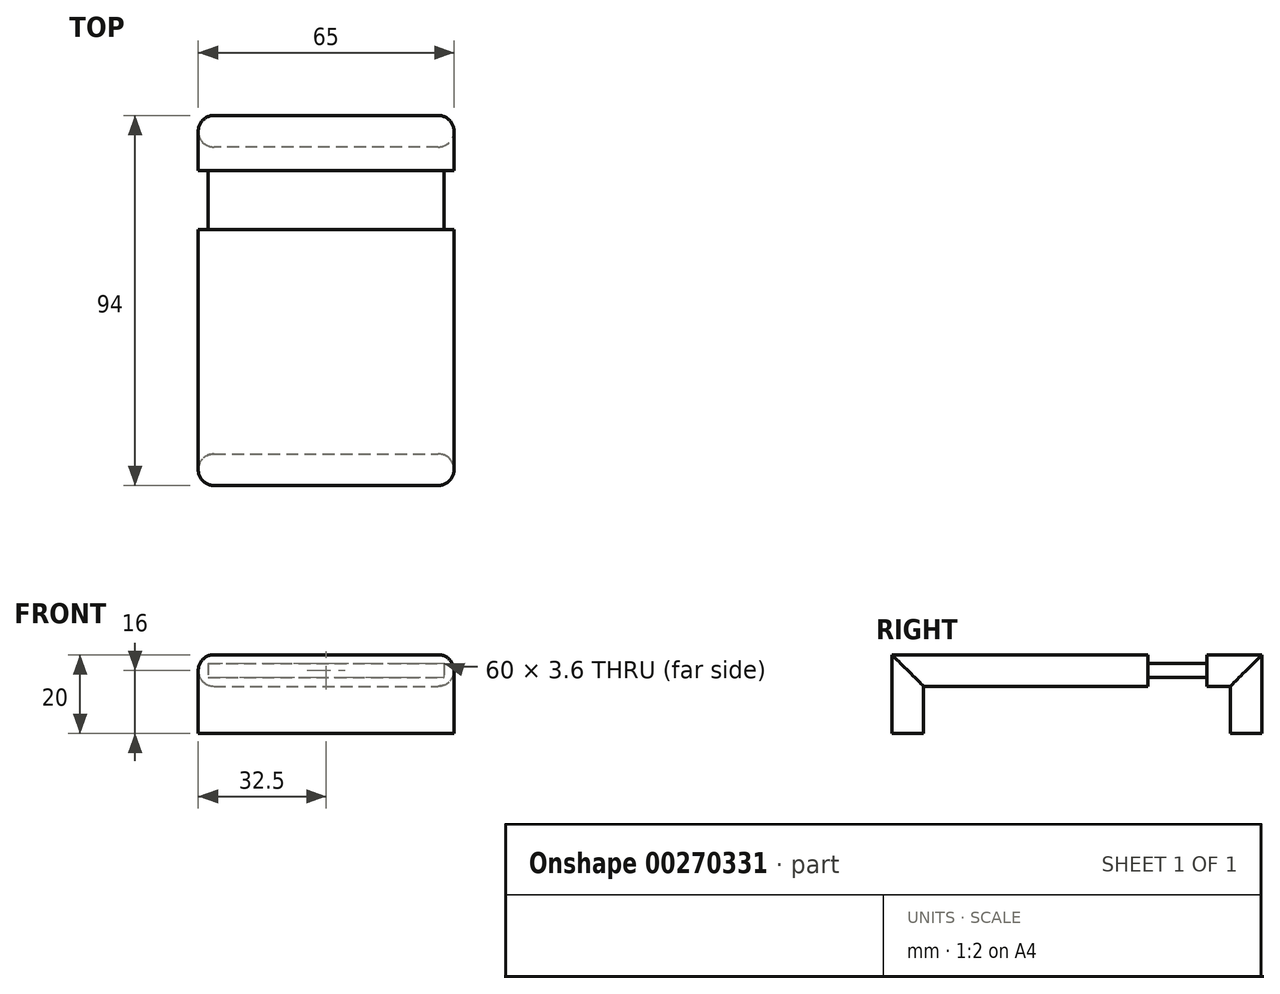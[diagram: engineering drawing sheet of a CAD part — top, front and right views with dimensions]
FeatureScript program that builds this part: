
annotation { "Feature Type Name" : "Feature", "Feature Type Description" : "" }
export const myFeature = defineFeature(function(context is Context, id is Id, definition is map)
    precondition{}
    {
        {
            var Q0;
            Q0=qCreatedBy(makeId("Top.planeOp"),FACE);
            var sketch = newSketch(context, id + "F0", { "sketchPlane" : qUnion([Q0])});
            skLineSegment(sketch, "E0.bottom", {"start": v(32.5, -32.5) * mm, "end": v(-32.5, -32.5) * mm});
            skLineSegment(sketch, "E0.top", {"start": v(32.5, 32.5) * mm, "end": v(-32.5, 32.5) * mm});
            skLineSegment(sketch, "E0.left", {"start": v(32.5, -32.5) * mm, "end": v(32.5, 32.5) * mm});
            skLineSegment(sketch, "E0.right", {"start": v(-32.5, -32.5) * mm, "end": v(-32.5, 32.5) * mm});
            skPoint(sketch, "E0.middle", {"position": v(0, 0) * mm});
            skSolve(sketch);
        }
        {
            var Q0;
            Q0 = qSketchRegion(id + "F0", true);
            extrude(context, id + "F1", {"entities" : qUnion([Q0]), "depth" : 8 * mm});
        }
        {
            var Q0;
            Q0=makeQuery(id+"F1.opExtrude","SWEPT_FACE",FACE,{"disambiguationData":[OSD([sQuery(id+"F0.wireOp",EDGE,"E0.bottom")])]});
            var sketch = newSketch(context, id + "F2", { "sketchPlane" : qUnion([Q0])});
            skLineSegment(sketch, "E1.bottom", {"start": v(32.5, 8) * mm, "end": v(-32.5, 8) * mm});
            skLineSegment(sketch, "E1.top", {"start": v(32.5, -12) * mm, "end": v(-32.5, -12) * mm});
            skLineSegment(sketch, "E1.left", {"start": v(32.5, 8) * mm, "end": v(32.5, -12) * mm});
            skLineSegment(sketch, "E1.right", {"start": v(-32.5, 8) * mm, "end": v(-32.5, -12) * mm});
            skSolve(sketch);
        }
        {
            var Q0;
            Q0 = qSketchRegion(id + "F2", true);
            extrude(context, id + "F3", {"entities" : qUnion([Q0]), "operationType" : NewBodyOperationType.ADD, "oppositeDirection" : true, "depth" : 8 * mm});
        }
        {
            var Q0;
            Q0=makeQuery(id+"F1.opExtrude","SWEPT_FACE",FACE,{"disambiguationData":[OSD([sQuery(id+"F0.wireOp",EDGE,"E0.top")])]});
            var sketch = newSketch(context, id + "F4", { "sketchPlane" : qUnion([Q0])});
            skLineSegment(sketch, "E2.bottom", {"start": v(30, 5.8) * mm, "end": v(-30, 5.8) * mm});
            skLineSegment(sketch, "E2.top", {"start": v(30, 2.2) * mm, "end": v(-30, 2.2) * mm});
            skLineSegment(sketch, "E2.left", {"start": v(30, 5.8) * mm, "end": v(30, 2.2) * mm});
            skLineSegment(sketch, "E2.right", {"start": v(-30, 5.8) * mm, "end": v(-30, 2.2) * mm});
            skPoint(sketch, "E2.middle", {"position": v(0, 4) * mm});
            skPoint(sketch, "E2.middle.positionSnap0", {"position": v(-32.5, 4) * mm});
            skPoint(sketch, "E2.middle.positionSnap1", {"position": v(0, 8) * mm});
            skPoint(sketch, "E2.centerSnap0", {"position": v(-32.5, 4) * mm});
            skPoint(sketch, "E2.centerSnap1", {"position": v(0, 8) * mm});
            skSolve(sketch);
        }
        {
            var Q0;
            Q0 = qSketchRegion(id + "F4", true);
            extrude(context, id + "F5", {"entities" : qUnion([Q0]), "operationType" : NewBodyOperationType.ADD, "depth" : 15 * mm});
        }
        {
            var Q0;
            Q0=makeQuery(id+"F3.opExtrude","CAP_EDGE",EDGE,{"disambiguationData":[OSD([sQuery(id+"F2.wireOp",EDGE,"E1.right")])],"isStart":false});
            var Q1;
            Q1=makeQuery(id+"F3.boolean.opBoolean","MERGE",EDGE,{"derivedFrom":[makeQuery(id+"F1.opExtrude","SWEPT_EDGE",EDGE,{"disambiguationData":[OSD([sQuery(id+"F0.wireOp",EDGE,"E0.bottom"),sQuery(id+"F0.wireOp",EDGE,"E0.right")])]}),makeQuery(id+"F3.opExtrude","CAP_EDGE",EDGE,{"disambiguationData":[OSD([sQuery(id+"F2.wireOp",EDGE,"E1.right")])],"isStart":true})]});
            var Q2;
            Q2=makeQuery(id+"F3.opExtrude","CAP_EDGE",EDGE,{"disambiguationData":[OSD([sQuery(id+"F2.wireOp",EDGE,"E1.left")])],"isStart":false});
            var Q3;
            Q3=makeQuery(id+"F3.boolean.opBoolean","MERGE",EDGE,{"derivedFrom":[makeQuery(id+"F1.opExtrude","SWEPT_EDGE",EDGE,{"disambiguationData":[OSD([sQuery(id+"F0.wireOp",EDGE,"E0.bottom"),sQuery(id+"F0.wireOp",EDGE,"E0.left")])]}),makeQuery(id+"F3.opExtrude","CAP_EDGE",EDGE,{"disambiguationData":[OSD([sQuery(id+"F2.wireOp",EDGE,"E1.left")])],"isStart":true})]});
            var Q4;
            Q4=makeQuery(id+"F1.opExtrude","CAP_EDGE",EDGE,{"disambiguationData":[OSD([sQuery(id+"F0.wireOp",EDGE,"E0.left")])],"isStart":false});
            var Q5;
            Q5=makeQuery(id+"F1.opExtrude","CAP_EDGE",EDGE,{"disambiguationData":[OSD([sQuery(id+"F0.wireOp",EDGE,"E0.right")])],"isStart":false});
            var Q6;
            Q6=makeQuery(id+"F1.opExtrude","CAP_EDGE",EDGE,{"disambiguationData":[OSD([sQuery(id+"F0.wireOp",EDGE,"E0.left")])],"isStart":true});
            var Q7;
            Q7=makeQuery(id+"F1.opExtrude","CAP_EDGE",EDGE,{"disambiguationData":[OSD([sQuery(id+"F0.wireOp",EDGE,"E0.right")])],"isStart":true});
            fillet(context, id + "F6", {"entities" : qUnion([Q0, Q1, Q2, Q3, Q4, Q5, Q6, Q7]), "radius" : 4 * mm, "tangentPropagation" : true, "allowEdgeOverflow" : false});
        }
        {
            var Q0;
            Q0=makeQuery(id+"F5.opExtrude","CAP_FACE",FACE,{"disambiguationData":[OSD([sQuery(id+"F4.wireOp",EDGE,"E2.bottom"),sQuery(id+"F4.wireOp",EDGE,"E2.top"),sQuery(id+"F4.wireOp",EDGE,"E2.left"),sQuery(id+"F4.wireOp",EDGE,"E2.right")])],"isStart":false});
            var sketch = newSketch(context, id + "F7", { "sketchPlane" : qUnion([Q0])});
            skLineSegment(sketch, "E3.bottom", {"start": v(32.5, 8) * mm, "end": v(-32.5, 8) * mm});
            skLineSegment(sketch, "E3.top", {"start": v(32.5, 0) * mm, "end": v(-32.5, 0) * mm});
            skLineSegment(sketch, "E3.left", {"start": v(32.5, 8) * mm, "end": v(32.5, 0) * mm});
            skLineSegment(sketch, "E3.right", {"start": v(-32.5, 8) * mm, "end": v(-32.5, 0) * mm});
            skPoint(sketch, "E3.middle", {"position": v(0, 4) * mm});
            skPoint(sketch, "E3.middle.positionSnap0", {"position": v(-30, 4) * mm});
            skPoint(sketch, "E3.middle.positionSnap1", {"position": v(0, 5.8) * mm});
            skPoint(sketch, "E3.centerSnap0", {"position": v(-30, 4) * mm});
            skPoint(sketch, "E3.centerSnap1", {"position": v(0, 5.8) * mm});
            skSolve(sketch);
        }
        {
            var Q0;
            Q0 = qSketchRegion(id + "F7", true);
            extrude(context, id + "F8", {"entities" : qUnion([Q0]), "operationType" : NewBodyOperationType.ADD, "depth" : 14 * mm});
        }
        {
            var Q0;
            Q0=makeQuery(id+"F8.opExtrude","SWEPT_FACE",FACE,{"disambiguationData":[OSD([sQuery(id+"F7.wireOp",EDGE,"E3.top")])]});
            var sketch = newSketch(context, id + "F9", { "sketchPlane" : qUnion([Q0])});
            skLineSegment(sketch, "E4.bottom", {"start": v(32.5, -61.5) * mm, "end": v(-32.5, -61.5) * mm});
            skLineSegment(sketch, "E4.top", {"start": v(32.5, -53.5) * mm, "end": v(-32.5, -53.5) * mm});
            skLineSegment(sketch, "E4.left", {"start": v(32.5, -61.5) * mm, "end": v(32.5, -53.5) * mm});
            skLineSegment(sketch, "E4.right", {"start": v(-32.5, -61.5) * mm, "end": v(-32.5, -53.5) * mm});
            skSolve(sketch);
        }
        {
            var Q0;
            Q0 = qSketchRegion(id + "F9", true);
            var Q1;
            Q1=makeQuery(id+"F3.opExtrude","SWEPT_FACE",FACE,{"disambiguationData":[OSD([sQuery(id+"F2.wireOp",EDGE,"E1.top")])]});
            extrude(context, id + "F10", {"entities" : qUnion([Q0]), "operationType" : NewBodyOperationType.ADD, "endBound" : BoundingType.UP_TO_SURFACE, "endBoundEntityFace" : qUnion([Q1]), "depth" : 25 * mm});
        }
        {
            var Q0;
            Q0=makeQuery(id+"F10.boolean.opBoolean","MERGE",EDGE,{"derivedFrom":[makeQuery(id+"F8.opExtrude","CAP_EDGE",EDGE,{"disambiguationData":[OSD([sQuery(id+"F7.wireOp",EDGE,"E3.left")])],"isStart":false}),makeQuery(id+"F10.opExtrude","SWEPT_EDGE",EDGE,{"disambiguationData":[OSD([sQuery(id+"F9.wireOp",EDGE,"E4.bottom"),sQuery(id+"F9.wireOp",EDGE,"E4.right")])]})]});
            var Q1;
            Q1=makeQuery(id+"F10.opExtrude","SWEPT_EDGE",EDGE,{"disambiguationData":[OSD([sQuery(id+"F7.wireOp",EDGE,"E3.top"),sQuery(id+"F7.wireOp",EDGE,"E3.left"),sQuery(id+"F9.wireOp",EDGE,"E4.top"),sQuery(id+"F9.wireOp",EDGE,"E4.right")])]});
            var Q2;
            Q2=makeQuery(id+"F8.opExtrude","SWEPT_EDGE",EDGE,{"disambiguationData":[OSD([sQuery(id+"F7.wireOp",EDGE,"E3.top"),sQuery(id+"F7.wireOp",EDGE,"E3.left")])]});
            var Q3;
            Q3=makeQuery(id+"F8.opExtrude","SWEPT_EDGE",EDGE,{"disambiguationData":[OSD([sQuery(id+"F7.wireOp",EDGE,"E3.bottom"),sQuery(id+"F7.wireOp",EDGE,"E3.left")])]});
            var Q4;
            Q4=makeQuery(id+"F8.opExtrude","SWEPT_EDGE",EDGE,{"disambiguationData":[OSD([sQuery(id+"F7.wireOp",EDGE,"E3.top"),sQuery(id+"F7.wireOp",EDGE,"E3.right")])]});
            var Q5;
            Q5=makeQuery(id+"F8.opExtrude","SWEPT_EDGE",EDGE,{"disambiguationData":[OSD([sQuery(id+"F7.wireOp",EDGE,"E3.bottom"),sQuery(id+"F7.wireOp",EDGE,"E3.right")])]});
            var Q6;
            Q6=makeQuery(id+"F10.boolean.opBoolean","MERGE",EDGE,{"derivedFrom":[makeQuery(id+"F8.opExtrude","CAP_EDGE",EDGE,{"disambiguationData":[OSD([sQuery(id+"F7.wireOp",EDGE,"E3.right")])],"isStart":false}),makeQuery(id+"F10.opExtrude","SWEPT_EDGE",EDGE,{"disambiguationData":[OSD([sQuery(id+"F9.wireOp",EDGE,"E4.bottom"),sQuery(id+"F9.wireOp",EDGE,"E4.left")])]})]});
            var Q7;
            Q7=makeQuery(id+"F10.opExtrude","SWEPT_EDGE",EDGE,{"disambiguationData":[OSD([sQuery(id+"F7.wireOp",EDGE,"E3.top"),sQuery(id+"F7.wireOp",EDGE,"E3.right"),sQuery(id+"F9.wireOp",EDGE,"E4.top"),sQuery(id+"F9.wireOp",EDGE,"E4.left")])]});
            fillet(context, id + "F11", {"entities" : qUnion([Q0, Q1, Q2, Q3, Q4, Q5, Q6, Q7]), "radius" : 4 * mm, "tangentPropagation" : true, "allowEdgeOverflow" : false});
        }
    });
